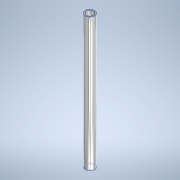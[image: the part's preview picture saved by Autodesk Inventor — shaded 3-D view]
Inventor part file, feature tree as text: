
AUTODESK INVENTOR PART (.ipt)
format: ipt  version: 2020.3 (Build 243373000, 373)  size: 100,352 bytes
history: native  units: mm
features: sketch x2, other x1, extrude x1, hole x1
ambient origin geometry x8: Origin, YZ Plane, XZ Plane, XY Plane, X Axis, Y Axis, Z Axis, Center Point
bodies: Body1 (feature_tree)
feature tree (5):
  other  "ソリッド1"
  extrude  "押し出し1"  Depth=4.0mm
  hole  "穴1"  [1 undecoded]
  sketch  "スケッチ1"
  sketch  "スケッチ2"
note: 1 required parameter value undecoded (feature->parameter linkage not recoverable at this tier; creation-order binding heuristic only, values carry confidence <= 0.55)
